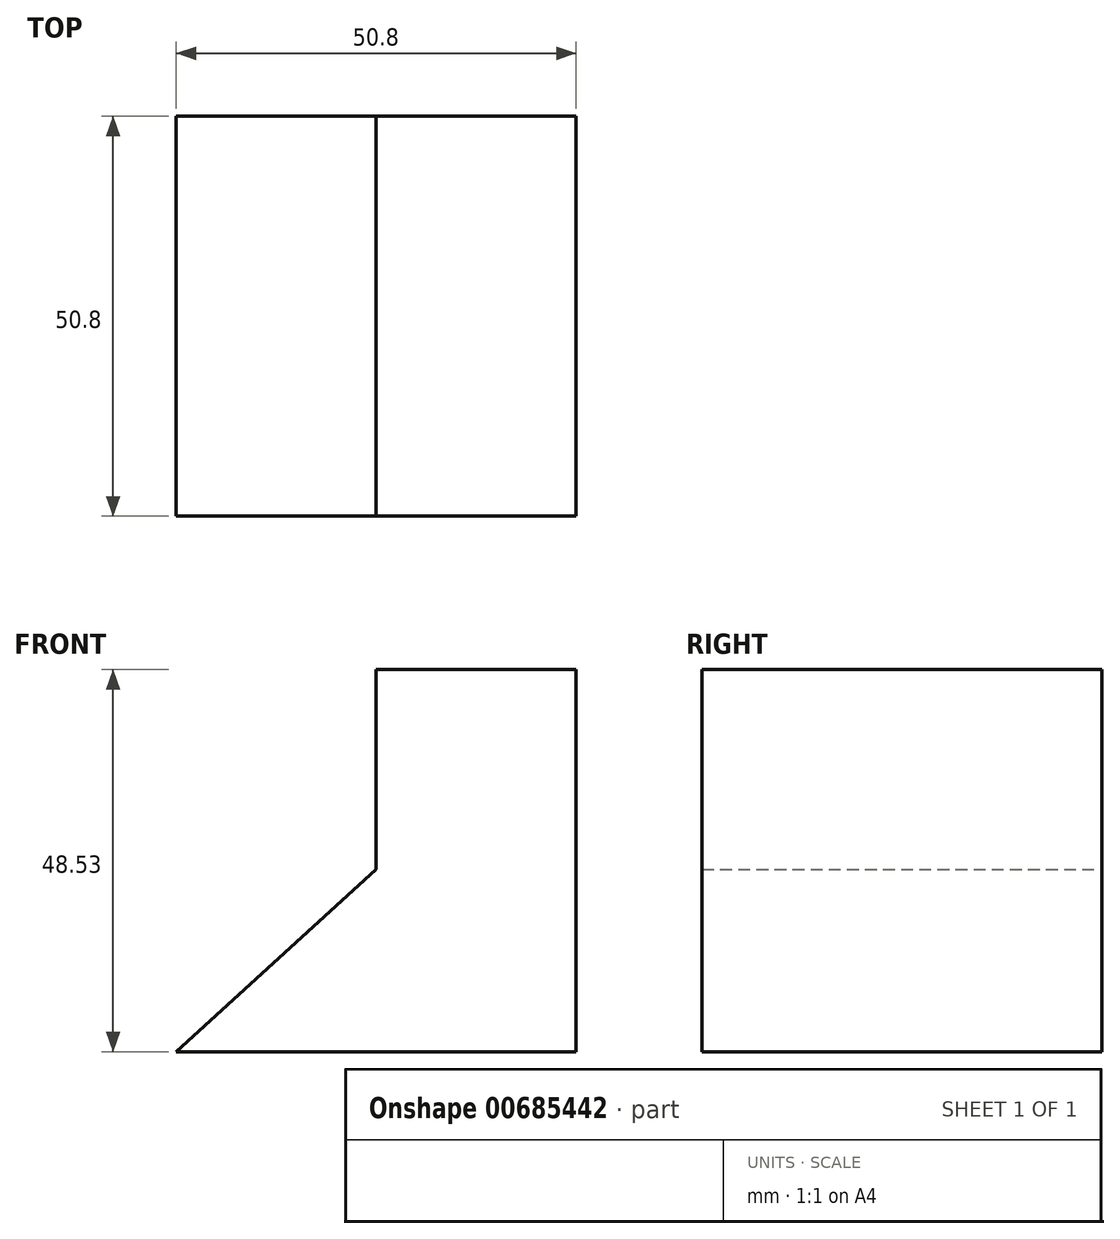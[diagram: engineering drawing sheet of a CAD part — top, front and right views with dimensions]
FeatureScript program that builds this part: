
annotation { "Feature Type Name" : "Feature", "Feature Type Description" : "" }
export const myFeature = defineFeature(function(context is Context, id is Id, definition is map)
    precondition{}
    {
        {
            var Q0;
            Q0=qCreatedBy(makeId("Front.planeOp"),FACE);
            var sketch = newSketch(context, id + "F0", { "sketchPlane" : qUnion([Q0])});
            skLineSegment(sketch, "E0", {"start": v(0, 48.53) * mm, "end": v(0, -2.27) * mm});
            skLineSegment(sketch, "E1", {"start": v(0, 48.53) * mm, "end": v(-25.4, 48.53) * mm});
            skLineSegment(sketch, "E2", {"start": v(-25.4, 48.53) * mm, "end": v(-25.4, 23.13) * mm});
            skLineSegment(sketch, "E3", {"start": v(0, 0) * mm, "end": v(-50.8, 0) * mm});
            skLineSegment(sketch, "E4", {"start": v(-25.4, 23.13) * mm, "end": v(-50.8, 0) * mm});
            skSolve(sketch);
        }
        {
            var Q0;
            Q0 = qSketchRegion(id + "F0", true);
            extrude(context, id + "F1", {"entities" : qUnion([Q0]), "depth" : 50.8 * mm, "offsetDistance" : 25.4 * mm});
        }
    });
